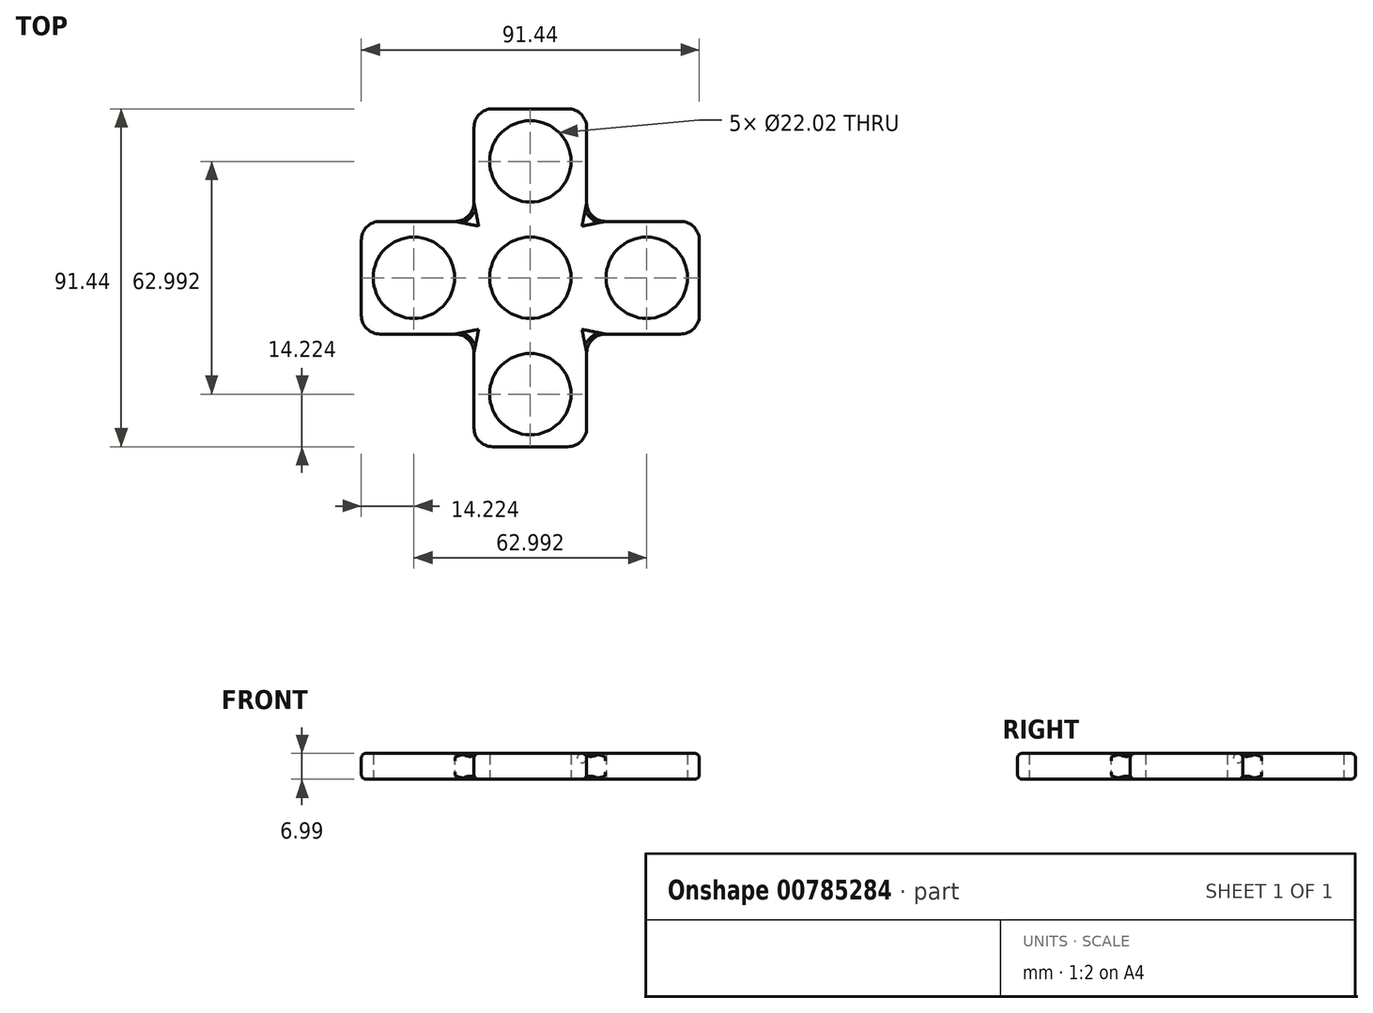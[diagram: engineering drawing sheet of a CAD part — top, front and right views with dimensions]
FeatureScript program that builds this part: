
annotation { "Feature Type Name" : "Feature", "Feature Type Description" : "" }
export const myFeature = defineFeature(function(context is Context, id is Id, definition is map)
    precondition{}
    {
        {
            var Q0;
            Q0=qCreatedBy(makeId("Top.planeOp"),FACE);
            var sketch = newSketch(context, id + "F0", { "sketchPlane" : qUnion([Q0])});
            skCircle(sketch, "E0", {"center": v(0, 0) * mm, "radius": 11.01 * mm});
            skCircle(sketch, "E1", {"center": v(0, 0) * mm, "radius": 18.87 * mm});
            skLineSegment(sketch, "E2", {"start": v(-15.24, 11.13) * mm, "end": v(-15.24, 45.72) * mm});
            skLineSegment(sketch, "E3", {"start": v(-15.24, 45.72) * mm, "end": v(15.24, 45.72) * mm});
            skLineSegment(sketch, "E4", {"start": v(15.24, 45.72) * mm, "end": v(15.24, 11.13) * mm});
            skLineSegment(sketch, "E5.1.0", {"start": v(-45.72, -15.24) * mm, "end": v(-45.72, 15.24) * mm});
            skLineSegment(sketch, "E5.1.1", {"start": v(-11.13, -15.24) * mm, "end": v(-45.72, -15.24) * mm});
            skLineSegment(sketch, "E5.1.2", {"start": v(-45.72, 15.24) * mm, "end": v(-11.13, 15.24) * mm});
            skLineSegment(sketch, "E5.2.0", {"start": v(15.24, -45.72) * mm, "end": v(-15.24, -45.72) * mm});
            skLineSegment(sketch, "E5.2.1", {"start": v(15.24, -11.13) * mm, "end": v(15.24, -45.72) * mm});
            skLineSegment(sketch, "E5.2.2", {"start": v(-15.24, -45.72) * mm, "end": v(-15.24, -11.13) * mm});
            skLineSegment(sketch, "E5.3.0", {"start": v(45.72, 15.24) * mm, "end": v(45.72, -15.24) * mm});
            skLineSegment(sketch, "E5.3.1", {"start": v(11.13, 15.24) * mm, "end": v(45.72, 15.24) * mm});
            skLineSegment(sketch, "E5.3.2", {"start": v(45.72, -15.24) * mm, "end": v(11.13, -15.24) * mm});
            skCircle(sketch, "E6", {"center": v(0, -31.5) * mm, "radius": 11.01 * mm});
            skCircle(sketch, "E7", {"center": v(-31.5, 0) * mm, "radius": 11.01 * mm});
            skCircle(sketch, "E8", {"center": v(31.5, 0) * mm, "radius": 11.01 * mm});
            skCircle(sketch, "E9", {"center": v(0, 31.5) * mm, "radius": 11.01 * mm});
            skLineSegment(sketch, "E10", {"start": v(0, 0) * mm, "end": v(-31.5, 0) * mm});
            skLineSegment(sketch, "E11", {"start": v(0, 0) * mm, "end": v(0, -31.5) * mm});
            skLineSegment(sketch, "E12", {"start": v(0, 0) * mm, "end": v(31.5, 0) * mm});
            skLineSegment(sketch, "E13", {"start": v(0, 0) * mm, "end": v(0, 31.5) * mm});
            skSolve(sketch);
        }
        {
            var Q0;
            Q0=qSketchRegion(id+"F0",true);
            var Q1;
            {var subQ5=sQuery(id+"F0.wireOp",EDGE,"E0");var subQ7=sQuery(id+"F0.wireOp",EDGE,"E13");var subQ9=makeQuery(id+"F0.imprint","INTERSECT",VERTEX,{"derivedFrom":[subQ5,subQ7]});Q1=makeQuery(id+"F0.imprint","IMPRINT",FACE,{"disambiguationData":[TD([[makeQuery(id+"F0.imprint","IMPRINT",EDGE,{"disambiguationData":[TD([[subQ9,-1.0]])],"derivedFrom":subQ5}),-1.0]])]});}
            var Q2;
            {var subQ2=sQuery(id+"F0.wireOp",EDGE,"E13");var subQ7=sQuery(id+"F0.wireOp",EDGE,"E0");var subQ8=makeQuery(id+"F0.imprint","INTERSECT",VERTEX,{"derivedFrom":[subQ7,subQ2]});Q2=makeQuery(id+"F0.imprint","IMPRINT",FACE,{"disambiguationData":[TD([[makeQuery(id+"F0.imprint","IMPRINT",EDGE,{"disambiguationData":[TD([[subQ8,1.0]])],"derivedFrom":subQ7}),-1.0]])]});}
            var Q3;
            {var subQ2=sQuery(id+"F0.wireOp",EDGE,"E12");var subQ5=sQuery(id+"F0.wireOp",EDGE,"E0");var subQ6=makeQuery(id+"F0.imprint","INTERSECT",VERTEX,{"derivedFrom":[subQ5,subQ2]});Q3=makeQuery(id+"F0.imprint","IMPRINT",FACE,{"disambiguationData":[TD([[makeQuery(id+"F0.imprint","IMPRINT",EDGE,{"disambiguationData":[TD([[subQ6,1.0]])],"derivedFrom":subQ5}),-1.0]])]});}
            var Q4;
            {var subQ3=sQuery(id+"F0.wireOp",EDGE,"E10");var subQ7=sQuery(id+"F0.wireOp",EDGE,"E0");var subQ9=makeQuery(id+"F0.imprint","INTERSECT",VERTEX,{"derivedFrom":[subQ7,subQ3]});Q4=makeQuery(id+"F0.imprint","IMPRINT",FACE,{"disambiguationData":[TD([[makeQuery(id+"F0.imprint","IMPRINT",EDGE,{"disambiguationData":[TD([[subQ9,-1.0]])],"derivedFrom":subQ7}),-1.0]])]});}
            extrude(context, id + "F1", {"entities" : qUnion([Q0, Q1, Q2, Q3, Q4]), "depth" : 7 * mm, "offsetDistance" : 25.4 * mm});
        }
        {
            var Q0;
            Q0=makeQuery(id+"F1.opExtrude","CAP_EDGE",EDGE,{"disambiguationData":[OSD([sQuery(id+"F0.wireOp",EDGE,"E5.2.2")])],"isStart":true});
            var Q1;
            Q1=makeQuery(id+"F1.opExtrude","CAP_EDGE",EDGE,{"disambiguationData":[OSD([sQuery(id+"F0.wireOp",EDGE,"E5.2.0")])],"isStart":true});
            var Q2;
            Q2=makeQuery(id+"F1.opExtrude","CAP_EDGE",EDGE,{"disambiguationData":[OSD([sQuery(id+"F0.wireOp",EDGE,"E5.2.1")])],"isStart":true});
            var Q3;
            Q3=makeQuery(id+"F1.opExtrude","CAP_EDGE",EDGE,{"disambiguationData":[OSD([sQuery(id+"F0.wireOp",EDGE,"E5.3.2")])],"isStart":true});
            var Q4;
            Q4=makeQuery(id+"F1.opExtrude","CAP_EDGE",EDGE,{"disambiguationData":[OSD([sQuery(id+"F0.wireOp",EDGE,"E5.3.0")])],"isStart":true});
            var Q5;
            Q5=makeQuery(id+"F1.opExtrude","CAP_EDGE",EDGE,{"disambiguationData":[OSD([sQuery(id+"F0.wireOp",EDGE,"E5.3.1")])],"isStart":true});
            var Q6;
            Q6=makeQuery(id+"F1.opExtrude","CAP_EDGE",EDGE,{"disambiguationData":[OSD([sQuery(id+"F0.wireOp",EDGE,"E4")])],"isStart":true});
            var Q7;
            Q7=makeQuery(id+"F1.opExtrude","CAP_EDGE",EDGE,{"disambiguationData":[OSD([sQuery(id+"F0.wireOp",EDGE,"E3")])],"isStart":true});
            var Q8;
            Q8=makeQuery(id+"F1.opExtrude","CAP_EDGE",EDGE,{"disambiguationData":[OSD([sQuery(id+"F0.wireOp",EDGE,"E2")])],"isStart":true});
            var Q9;
            Q9=makeQuery(id+"F1.opExtrude","CAP_EDGE",EDGE,{"disambiguationData":[OSD([sQuery(id+"F0.wireOp",EDGE,"E5.1.2")])],"isStart":true});
            var Q10;
            Q10=makeQuery(id+"F1.opExtrude","CAP_EDGE",EDGE,{"disambiguationData":[OSD([sQuery(id+"F0.wireOp",EDGE,"E5.1.0")])],"isStart":true});
            var Q11;
            Q11=makeQuery(id+"F1.opExtrude","CAP_EDGE",EDGE,{"disambiguationData":[OSD([sQuery(id+"F0.wireOp",EDGE,"E5.1.1")])],"isStart":true});
            fillet(context, id + "F2", {"entities" : qUnion([Q0, Q1, Q2, Q3, Q4, Q5, Q6, Q7, Q8, Q9, Q10, Q11]), "radius" : 1.27 * mm, "tangentPropagation" : true, "allowEdgeOverflow" : false});
        }
        {
            var Q0;
            Q0=makeQuery(id+"F1.opExtrude","CAP_EDGE",EDGE,{"disambiguationData":[OSD([sQuery(id+"F0.wireOp",EDGE,"E5.1.0")])],"isStart":false});
            var Q1;
            Q1=makeQuery(id+"F1.opExtrude","CAP_EDGE",EDGE,{"disambiguationData":[OSD([sQuery(id+"F0.wireOp",EDGE,"E5.1.2")])],"isStart":false});
            var Q2;
            Q2=makeQuery(id+"F1.opExtrude","CAP_EDGE",EDGE,{"disambiguationData":[OSD([sQuery(id+"F0.wireOp",EDGE,"E2")])],"isStart":false});
            var Q3;
            Q3=makeQuery(id+"F1.opExtrude","CAP_EDGE",EDGE,{"disambiguationData":[OSD([sQuery(id+"F0.wireOp",EDGE,"E3")])],"isStart":false});
            var Q4;
            Q4=makeQuery(id+"F1.opExtrude","CAP_EDGE",EDGE,{"disambiguationData":[OSD([sQuery(id+"F0.wireOp",EDGE,"E4")])],"isStart":false});
            var Q5;
            Q5=makeQuery(id+"F1.opExtrude","CAP_EDGE",EDGE,{"disambiguationData":[OSD([sQuery(id+"F0.wireOp",EDGE,"E5.3.1")])],"isStart":false});
            var Q6;
            Q6=makeQuery(id+"F1.opExtrude","CAP_EDGE",EDGE,{"disambiguationData":[OSD([sQuery(id+"F0.wireOp",EDGE,"E5.3.0")])],"isStart":false});
            var Q7;
            Q7=makeQuery(id+"F1.opExtrude","CAP_EDGE",EDGE,{"disambiguationData":[OSD([sQuery(id+"F0.wireOp",EDGE,"E5.3.2")])],"isStart":false});
            var Q8;
            Q8=makeQuery(id+"F1.opExtrude","CAP_EDGE",EDGE,{"disambiguationData":[OSD([sQuery(id+"F0.wireOp",EDGE,"E5.2.1")])],"isStart":false});
            var Q9;
            Q9=makeQuery(id+"F1.opExtrude","CAP_EDGE",EDGE,{"disambiguationData":[OSD([sQuery(id+"F0.wireOp",EDGE,"E5.2.0")])],"isStart":false});
            var Q10;
            Q10=makeQuery(id+"F1.opExtrude","CAP_EDGE",EDGE,{"disambiguationData":[OSD([sQuery(id+"F0.wireOp",EDGE,"E5.2.2")])],"isStart":false});
            var Q11;
            Q11=makeQuery(id+"F1.opExtrude","CAP_EDGE",EDGE,{"disambiguationData":[OSD([sQuery(id+"F0.wireOp",EDGE,"E5.1.1")])],"isStart":false});
            fillet(context, id + "F3", {"entities" : qUnion([Q0, Q1, Q2, Q3, Q4, Q5, Q6, Q7, Q8, Q9, Q10, Q11]), "radius" : 1.27 * mm, "tangentPropagation" : true, "allowEdgeOverflow" : false});
        }
        {
            var Q0;
            Q0=makeQuery(id+"F1.opExtrude","SWEPT_EDGE",EDGE,{"disambiguationData":[OSD([sQuery(id+"F0.wireOp",EDGE,"E2"),sQuery(id+"F0.wireOp",EDGE,"E5.1.2")])]});
            var Q1;
            Q1=makeQuery(id+"F1.opExtrude","SWEPT_EDGE",EDGE,{"disambiguationData":[OSD([sQuery(id+"F0.wireOp",EDGE,"E2"),sQuery(id+"F0.wireOp",EDGE,"E3")])]});
            var Q2;
            Q2=makeQuery(id+"F1.opExtrude","SWEPT_EDGE",EDGE,{"disambiguationData":[OSD([sQuery(id+"F0.wireOp",EDGE,"E3"),sQuery(id+"F0.wireOp",EDGE,"E4")])]});
            var Q3;
            Q3=makeQuery(id+"F1.opExtrude","SWEPT_EDGE",EDGE,{"disambiguationData":[OSD([sQuery(id+"F0.wireOp",EDGE,"E5.1.0"),sQuery(id+"F0.wireOp",EDGE,"E5.1.2")])]});
            var Q4;
            Q4=makeQuery(id+"F1.opExtrude","SWEPT_EDGE",EDGE,{"disambiguationData":[OSD([sQuery(id+"F0.wireOp",EDGE,"E5.1.0"),sQuery(id+"F0.wireOp",EDGE,"E5.1.1")])]});
            var Q5;
            Q5=makeQuery(id+"F1.opExtrude","SWEPT_EDGE",EDGE,{"disambiguationData":[OSD([sQuery(id+"F0.wireOp",EDGE,"E5.2.0"),sQuery(id+"F0.wireOp",EDGE,"E5.2.2")])]});
            var Q6;
            Q6=makeQuery(id+"F1.opExtrude","SWEPT_EDGE",EDGE,{"disambiguationData":[OSD([sQuery(id+"F0.wireOp",EDGE,"E5.1.1"),sQuery(id+"F0.wireOp",EDGE,"E5.2.2")])]});
            var Q7;
            Q7=makeQuery(id+"F1.opExtrude","SWEPT_EDGE",EDGE,{"disambiguationData":[OSD([sQuery(id+"F0.wireOp",EDGE,"E5.2.0"),sQuery(id+"F0.wireOp",EDGE,"E5.2.1")])]});
            var Q8;
            Q8=makeQuery(id+"F1.opExtrude","SWEPT_EDGE",EDGE,{"disambiguationData":[OSD([sQuery(id+"F0.wireOp",EDGE,"E5.2.1"),sQuery(id+"F0.wireOp",EDGE,"E5.3.2")])]});
            var Q9;
            Q9=makeQuery(id+"F1.opExtrude","SWEPT_EDGE",EDGE,{"disambiguationData":[OSD([sQuery(id+"F0.wireOp",EDGE,"E5.3.0"),sQuery(id+"F0.wireOp",EDGE,"E5.3.2")])]});
            var Q10;
            Q10=makeQuery(id+"F1.opExtrude","SWEPT_EDGE",EDGE,{"disambiguationData":[OSD([sQuery(id+"F0.wireOp",EDGE,"E5.3.0"),sQuery(id+"F0.wireOp",EDGE,"E5.3.1")])]});
            var Q11;
            Q11=makeQuery(id+"F1.opExtrude","SWEPT_EDGE",EDGE,{"disambiguationData":[OSD([sQuery(id+"F0.wireOp",EDGE,"E4"),sQuery(id+"F0.wireOp",EDGE,"E5.3.1")])]});
            fillet(context, id + "F4", {"entities" : qUnion([Q0, Q1, Q2, Q3, Q4, Q5, Q6, Q7, Q8, Q9, Q10, Q11]), "radius" : 5.08 * mm, "tangentPropagation" : true, "allowEdgeOverflow" : false});
        }
    });
